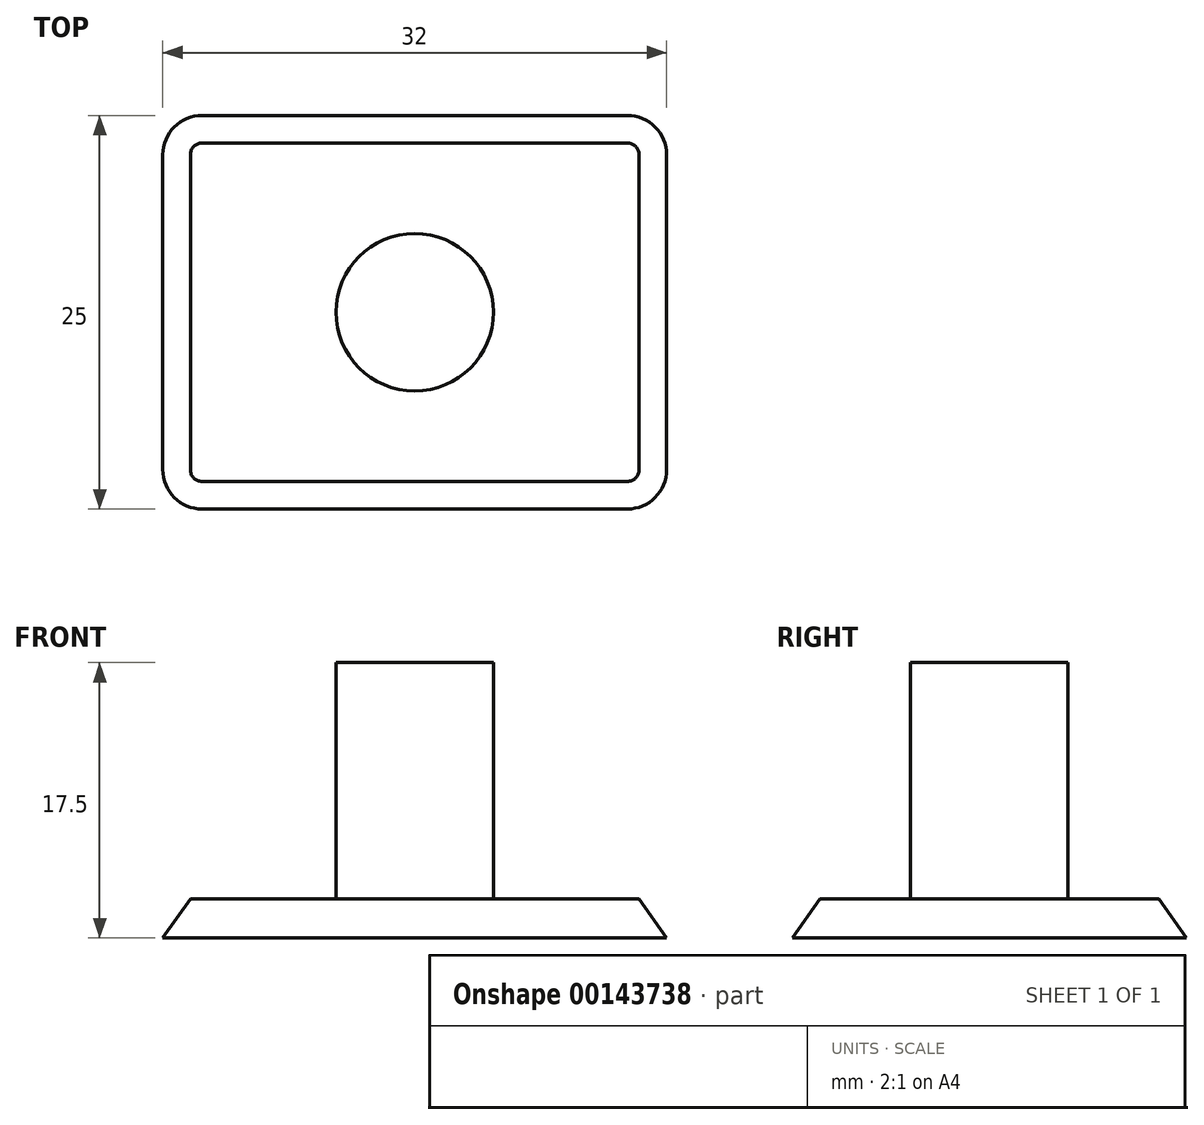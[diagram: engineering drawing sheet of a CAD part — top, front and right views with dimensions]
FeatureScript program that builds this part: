
annotation { "Feature Type Name" : "Feature", "Feature Type Description" : "" }
export const myFeature = defineFeature(function(context is Context, id is Id, definition is map)
    precondition{}
    {
        {
            var Q0;
            Q0=qCreatedBy(makeId("Top.planeOp"),FACE);
            var sketch = newSketch(context, id + "F0", { "sketchPlane" : qUnion([Q0])});
            skLineSegment(sketch, "E0.bottom", {"start": v(-16, 12.5) * mm, "end": v(16, 12.5) * mm});
            skLineSegment(sketch, "E0.top", {"start": v(-16, -12.5) * mm, "end": v(16, -12.5) * mm});
            skLineSegment(sketch, "E0.left", {"start": v(-16, 12.5) * mm, "end": v(-16, -12.5) * mm});
            skLineSegment(sketch, "E0.right", {"start": v(16, 12.5) * mm, "end": v(16, -12.5) * mm});
            skPoint(sketch, "E0.middle", {"position": v(0, 0) * mm});
            skCircle(sketch, "E1", {"center": v(0, 0) * mm, "radius": 5 * mm});
            skSolve(sketch);
        }
        {
            var Q0;
            Q0=makeQuery(id+"F0.imprint","IMPRINT",FACE,{"disambiguationData":[TD([[makeQuery(id+"F0.imprint","IMPRINT",EDGE,{"derivedFrom":sQuery(id+"F0.wireOp",EDGE,"E0.bottom")}),-1.0]])]});
            extrude(context, id + "F1", {"entities" : qUnion([Q0]), "depth" : 2.5 * mm});
        }
        {
            var Q0;
            Q0=makeQuery(id+"F1.opExtrude","SWEPT_EDGE",EDGE,{"disambiguationData":[OSD([sQuery(id+"F0.wireOp",EDGE,"E0.top"),sQuery(id+"F0.wireOp",EDGE,"E0.left")])]});
            var Q1;
            Q1=makeQuery(id+"F1.opExtrude","SWEPT_EDGE",EDGE,{"disambiguationData":[OSD([sQuery(id+"F0.wireOp",EDGE,"E0.top"),sQuery(id+"F0.wireOp",EDGE,"E0.right")])]});
            var Q2;
            Q2=makeQuery(id+"F1.opExtrude","SWEPT_EDGE",EDGE,{"disambiguationData":[OSD([sQuery(id+"F0.wireOp",EDGE,"E0.bottom"),sQuery(id+"F0.wireOp",EDGE,"E0.right")])]});
            var Q3;
            Q3=makeQuery(id+"F1.opExtrude","SWEPT_EDGE",EDGE,{"disambiguationData":[OSD([sQuery(id+"F0.wireOp",EDGE,"E0.bottom"),sQuery(id+"F0.wireOp",EDGE,"E0.left")])]});
            fillet(context, id + "F2", {"entities" : qUnion([Q0, Q1, Q2, Q3]), "radius" : 2.5 * mm, "tangentPropagation" : true, "allowEdgeOverflow" : false});
        }
        {
            var Q0;
            Q0=makeQuery(id+"F1.opExtrude","CAP_EDGE",EDGE,{"disambiguationData":[OSD([sQuery(id+"F0.wireOp",EDGE,"E0.top")])],"isStart":false});
            var Q1;
            Q1=makeQuery(id+"F1.opExtrude","CAP_EDGE",EDGE,{"disambiguationData":[OSD([sQuery(id+"F0.wireOp",EDGE,"E0.left")])],"isStart":false});
            var Q2;
            {var subQ0=sQuery(id+"F0.wireOp",EDGE,"E0.right");var subQ1=sQuery(id+"F0.wireOp",EDGE,"E0.top");Q2=makeQuery(id+"F2.opFillet","BLEND_EDGE",EDGE,{"blendedFrom":[makeQuery(id+"F1.opExtrude","SWEPT_EDGE",EDGE,{"disambiguationData":[OSD([subQ1,subQ0])]}),makeQuery(id+"F1.opExtrude","CAP_FACE",FACE,{"disambiguationData":[OSD([sQuery(id+"F0.wireOp",EDGE,"E0.bottom"),subQ1,sQuery(id+"F0.wireOp",EDGE,"E0.left"),subQ0])],"isStart":false})],"blendedInto":[makeQuery(id+"F1.opExtrude","CAP_FACE",FACE,{"disambiguationData":[OSD([sQuery(id+"F0.wireOp",EDGE,"E0.bottom"),subQ1,sQuery(id+"F0.wireOp",EDGE,"E0.left"),subQ0])],"isStart":false})]});}
            var Q3;
            Q3=makeQuery(id+"F1.opExtrude","CAP_EDGE",EDGE,{"disambiguationData":[OSD([sQuery(id+"F0.wireOp",EDGE,"E0.right")])],"isStart":false});
            var Q4;
            {var subQ0=sQuery(id+"F0.wireOp",EDGE,"E0.right");var subQ1=sQuery(id+"F0.wireOp",EDGE,"E0.bottom");Q4=makeQuery(id+"F2.opFillet","BLEND_EDGE",EDGE,{"blendedFrom":[makeQuery(id+"F1.opExtrude","SWEPT_EDGE",EDGE,{"disambiguationData":[OSD([subQ1,subQ0])]}),makeQuery(id+"F1.opExtrude","CAP_FACE",FACE,{"disambiguationData":[OSD([subQ1,sQuery(id+"F0.wireOp",EDGE,"E0.top"),sQuery(id+"F0.wireOp",EDGE,"E0.left"),subQ0])],"isStart":false})],"blendedInto":[makeQuery(id+"F1.opExtrude","CAP_FACE",FACE,{"disambiguationData":[OSD([subQ1,sQuery(id+"F0.wireOp",EDGE,"E0.top"),sQuery(id+"F0.wireOp",EDGE,"E0.left"),subQ0])],"isStart":false})]});}
            var Q5;
            Q5=makeQuery(id+"F1.opExtrude","CAP_EDGE",EDGE,{"disambiguationData":[OSD([sQuery(id+"F0.wireOp",EDGE,"E0.bottom")])],"isStart":false});
            var Q6;
            {var subQ0=sQuery(id+"F0.wireOp",EDGE,"E0.left");var subQ1=sQuery(id+"F0.wireOp",EDGE,"E0.bottom");Q6=makeQuery(id+"F2.opFillet","BLEND_EDGE",EDGE,{"blendedFrom":[makeQuery(id+"F1.opExtrude","SWEPT_EDGE",EDGE,{"disambiguationData":[OSD([subQ1,subQ0])]}),makeQuery(id+"F1.opExtrude","CAP_FACE",FACE,{"disambiguationData":[OSD([subQ1,sQuery(id+"F0.wireOp",EDGE,"E0.top"),subQ0,sQuery(id+"F0.wireOp",EDGE,"E0.right")])],"isStart":false})],"blendedInto":[makeQuery(id+"F1.opExtrude","CAP_FACE",FACE,{"disambiguationData":[OSD([subQ1,sQuery(id+"F0.wireOp",EDGE,"E0.top"),subQ0,sQuery(id+"F0.wireOp",EDGE,"E0.right")])],"isStart":false})]});}
            var Q7;
            {var subQ0=sQuery(id+"F0.wireOp",EDGE,"E0.left");var subQ1=sQuery(id+"F0.wireOp",EDGE,"E0.top");Q7=makeQuery(id+"F2.opFillet","BLEND_EDGE",EDGE,{"blendedFrom":[makeQuery(id+"F1.opExtrude","SWEPT_EDGE",EDGE,{"disambiguationData":[OSD([subQ1,subQ0])]}),makeQuery(id+"F1.opExtrude","CAP_FACE",FACE,{"disambiguationData":[OSD([sQuery(id+"F0.wireOp",EDGE,"E0.bottom"),subQ1,subQ0,sQuery(id+"F0.wireOp",EDGE,"E0.right")])],"isStart":false})],"blendedInto":[makeQuery(id+"F1.opExtrude","CAP_FACE",FACE,{"disambiguationData":[OSD([sQuery(id+"F0.wireOp",EDGE,"E0.bottom"),subQ1,subQ0,sQuery(id+"F0.wireOp",EDGE,"E0.right")])],"isStart":false})]});}
            chamfer(context, id + "F3", {"entities" : qUnion([Q0, Q1, Q2, Q3, Q4, Q5, Q6, Q7]), "chamferType" : ChamferType.OFFSET_ANGLE, "width" : 2.5 * mm, "oppositeDirection" : true, "angle" : 35 * degree, "tangentPropagation" : true});
        }
        {
            var Q0;
            Q0=makeQuery(id+"F0.imprint","IMPRINT",FACE,{"disambiguationData":[TD([[makeQuery(id+"F0.imprint","IMPRINT",EDGE,{"derivedFrom":sQuery(id+"F0.wireOp",EDGE,"E1")}),1.0]])]});
            extrude(context, id + "F4", {"entities" : qUnion([Q0]), "operationType" : NewBodyOperationType.ADD, "depth" : 17.5 * mm, "offsetDistance" : 25 * mm});
        }
    });
